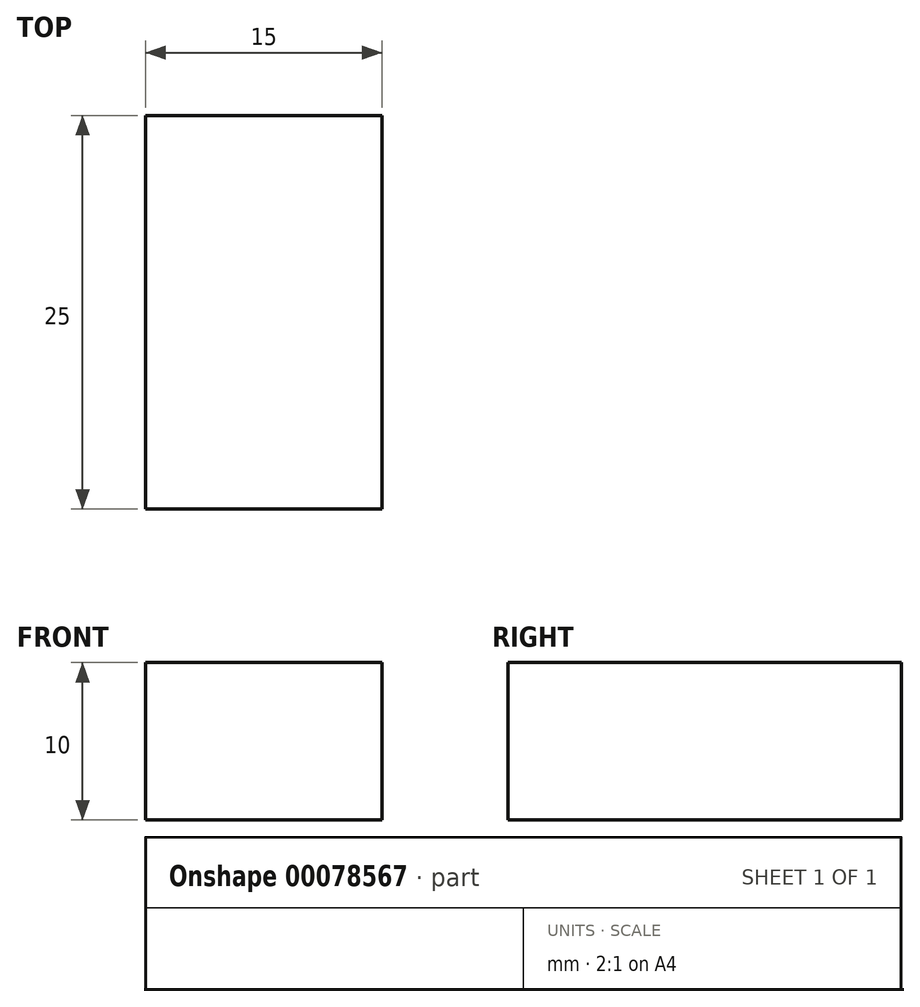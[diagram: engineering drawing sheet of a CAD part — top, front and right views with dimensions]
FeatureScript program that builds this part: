
annotation { "Feature Type Name" : "Feature", "Feature Type Description" : "" }
export const myFeature = defineFeature(function(context is Context, id is Id, definition is map)
    precondition{}
    {
        {
            var Q0;
            Q0=qCreatedBy(makeId("Front.planeOp"),FACE);
            var sketch = newSketch(context, id + "F0", { "sketchPlane" : qUnion([Q0])});
            skLineSegment(sketch, "E0", {"start": v(0, 0) * mm, "end": v(-150, 0) * mm});
            skLineSegment(sketch, "E1", {"start": v(-150, 0) * mm, "end": v(-206.02, -597.38) * mm});
            skLineSegment(sketch, "E2", {"start": v(-206.02, -597.38) * mm, "end": v(-226.02, -597.38) * mm});
            skLineSegment(sketch, "E3", {"start": v(-226.02, -597.38) * mm, "end": v(-166.72, 34.93) * mm});
            skLineSegment(sketch, "E4", {"start": v(-206.02, -597.38) * mm, "end": v(-140.62, 100.06) * mm, "construction": true});
            skLineSegment(sketch, "E5", {"start": v(-166.72, 34.93) * mm, "end": v(-146.72, 34.93) * mm, "construction": true});
            skLineSegment(sketch, "E6", {"start": v(0, 0) * mm, "end": v(0, 20) * mm, "construction": true});
            skLineSegment(sketch, "E7", {"start": v(0, 20) * mm, "end": v(-148.12, 20) * mm});
            skLineSegment(sketch, "E8", {"start": v(-148.12, 20) * mm, "end": v(-146.72, 34.93) * mm});
            skLineSegment(sketch, "E9", {"start": v(-146.72, 34.93) * mm, "end": v(-166.72, 34.93) * mm});
            skLineSegment(sketch, "E10.MirrorCS", {"start": v(166.72, 34.93) * mm, "end": v(146.72, 34.93) * mm, "construction": true});
            skLineSegment(sketch, "E11.MirrorCS", {"start": v(148.12, 20) * mm, "end": v(146.72, 34.93) * mm});
            skLineSegment(sketch, "E12.MirrorCS", {"start": v(146.72, 34.93) * mm, "end": v(166.72, 34.93) * mm});
            skLineSegment(sketch, "E13.MirrorCS", {"start": v(206.02, -597.38) * mm, "end": v(226.02, -597.38) * mm});
            skLineSegment(sketch, "E14.MirrorCS", {"start": v(206.02, -597.38) * mm, "end": v(140.62, 100.06) * mm, "construction": true});
            skLineSegment(sketch, "E15.MirrorCS", {"start": v(150, 0) * mm, "end": v(206.02, -597.38) * mm});
            skLineSegment(sketch, "E16.MirrorCS", {"start": v(226.02, -597.38) * mm, "end": v(166.72, 34.93) * mm});
            skLineSegment(sketch, "E17.MirrorCS", {"start": v(0, 0) * mm, "end": v(150, 0) * mm});
            skLineSegment(sketch, "E18.MirrorCS", {"start": v(0, 20) * mm, "end": v(148.12, 20) * mm});
            skPoint(sketch, "E19.oppositeSnap0", {"position": v(0, 10) * mm});
            skLineSegment(sketch, "E19.bottom", {"start": v(0, 0) * mm, "end": v(-15, 0) * mm});
            skLineSegment(sketch, "E19.top", {"start": v(0, 10) * mm, "end": v(-15, 10) * mm});
            skLineSegment(sketch, "E19.left", {"start": v(0, 0) * mm, "end": v(0, 10) * mm});
            skLineSegment(sketch, "E19.right", {"start": v(-15, 0) * mm, "end": v(-15, 10) * mm});
            skLineSegment(sketch, "E20.bottom", {"start": v(0, 10) * mm, "end": v(15, 10) * mm});
            skLineSegment(sketch, "E20.top", {"start": v(0, 0) * mm, "end": v(15, 0) * mm});
            skLineSegment(sketch, "E20.left", {"start": v(0, 10) * mm, "end": v(0, 0) * mm});
            skLineSegment(sketch, "E20.right", {"start": v(15, 10) * mm, "end": v(15, 0) * mm});
            skSolve(sketch);
        }
        {
            var Q0;
            Q0=makeQuery(id+"F0.imprint","IMPRINT",FACE,{"disambiguationData":[TD([[makeQuery(id+"F0.imprint","IMPRINT",EDGE,{"derivedFrom":sQuery(id+"F0.wireOp",EDGE,"E0")}),-1.0]])]});
            extrude(context, id + "F1", {"entities" : qUnion([Q0]), "depth" : 25 * mm});
        }
    });
